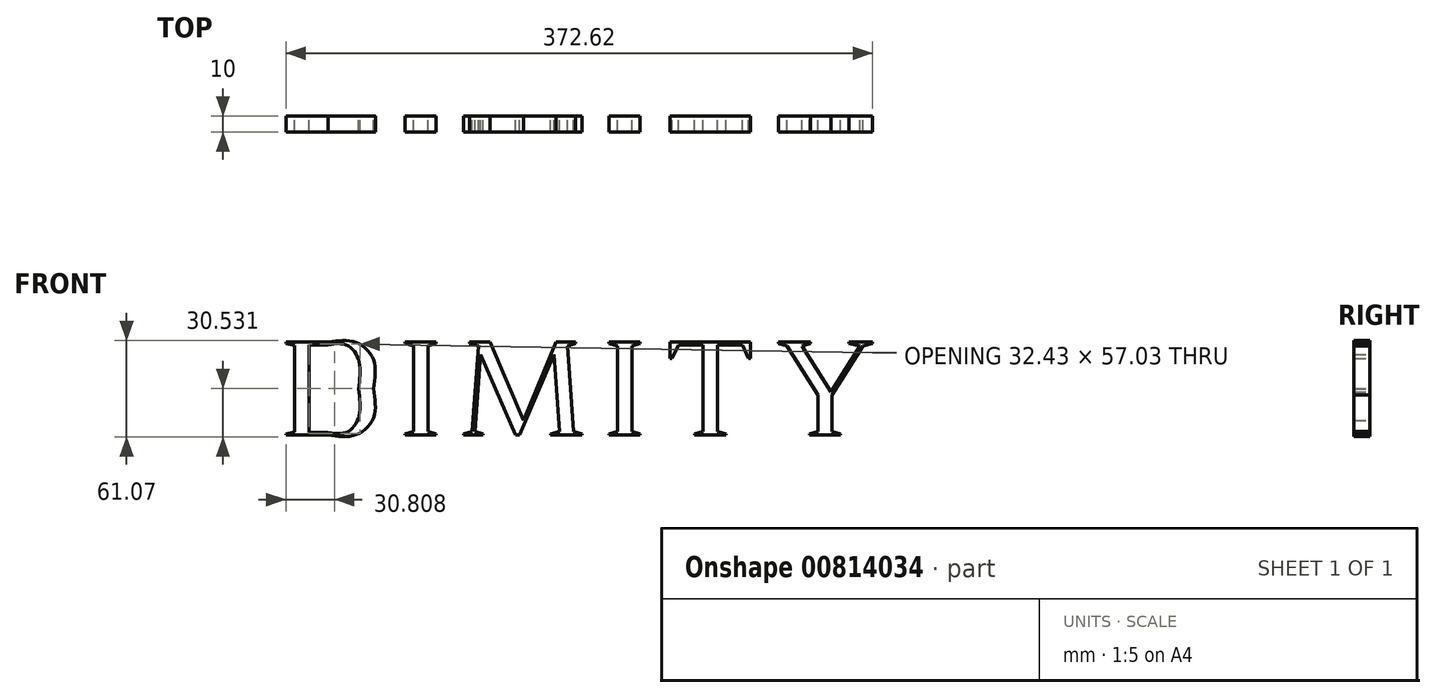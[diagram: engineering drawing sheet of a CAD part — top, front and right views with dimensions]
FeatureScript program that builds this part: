
annotation { "Feature Type Name" : "Feature", "Feature Type Description" : "" }
export const myFeature = defineFeature(function(context is Context, id is Id, definition is map)
    precondition{}
    {
        {
            var Q0;
            Q0=qCreatedBy(makeId("Front.planeOp"),FACE);
            var sketch = newSketch(context, id + "F0", { "sketchPlane" : qUnion([Q0])});
            skLineSegment(sketch, "E0", {"start": v(-186.3, 70.11) * mm, "end": v(-186.3, 69.35) * mm});
            skLineSegment(sketch, "E1", {"start": v(-186.3, 69.35) * mm, "end": v(-180.83, 68.09) * mm});
            skLineSegment(sketch, "E2", {"start": v(-180.83, 68.09) * mm, "end": v(-180.83, 13.09) * mm});
            skLineSegment(sketch, "E3", {"start": v(-180.83, 13.09) * mm, "end": v(-186.3, 11.74) * mm});
            skLineSegment(sketch, "E4", {"start": v(-186.3, 11.74) * mm, "end": v(-186.3, 11.06) * mm});
            skLineSegment(sketch, "E5", {"start": v(-186.3, 11.06) * mm, "end": v(-159.4, 11.06) * mm});
            skFitSpline(sketch, "E6", {"points": [v(-159.4, 11.06) * mm, v(-142.53, 11.06) * mm, v(-130.72, 22.03) * mm, v(-130.72, 40.59) * mm]});
            skFitSpline(sketch, "E7", {"points": [v(-130.72, 40.59) * mm, v(-130.72, 58.98) * mm, v(-142.53, 70.11) * mm, v(-159.4, 70.11) * mm]});
            skLineSegment(sketch, "E8", {"start": v(-159.4, 70.11) * mm, "end": v(-186.3, 70.11) * mm});
            skLineSegment(sketch, "E9", {"start": v(-171.72, 68.43) * mm, "end": v(-159.4, 68.43) * mm});
            skFitSpline(sketch, "E10", {"points": [v(-159.4, 68.43) * mm, v(-148.26, 68.43) * mm, v(-140.25, 59.15) * mm, v(-140.25, 40.5) * mm]});
            skFitSpline(sketch, "E11", {"points": [v(-140.25, 40.5) * mm, v(-140.25, 21.95) * mm, v(-148.26, 12.75) * mm, v(-159.4, 12.75) * mm]});
            skLineSegment(sketch, "E12", {"start": v(-159.4, 12.75) * mm, "end": v(-171.72, 12.75) * mm});
            skLineSegment(sketch, "E13", {"start": v(-171.72, 12.75) * mm, "end": v(-171.72, 68.43) * mm});
            skLineSegment(sketch, "E14", {"start": v(-110.64, 70.11) * mm, "end": v(-110.64, 69.27) * mm});
            skLineSegment(sketch, "E15", {"start": v(-110.64, 69.27) * mm, "end": v(-105.15, 67.67) * mm});
            skLineSegment(sketch, "E16", {"start": v(-105.15, 67.67) * mm, "end": v(-105.15, 13.5) * mm});
            skLineSegment(sketch, "E17", {"start": v(-105.15, 13.5) * mm, "end": v(-110.64, 11.9) * mm});
            skLineSegment(sketch, "E18", {"start": v(-110.64, 11.9) * mm, "end": v(-110.64, 11.06) * mm});
            skLineSegment(sketch, "E19", {"start": v(-110.64, 11.06) * mm, "end": v(-90.98, 11.06) * mm});
            skLineSegment(sketch, "E20", {"start": v(-90.98, 11.06) * mm, "end": v(-90.98, 11.9) * mm});
            skLineSegment(sketch, "E21", {"start": v(-90.98, 11.9) * mm, "end": v(-96.21, 13.5) * mm});
            skLineSegment(sketch, "E22", {"start": v(-96.21, 13.5) * mm, "end": v(-96.21, 67.67) * mm});
            skLineSegment(sketch, "E23", {"start": v(-96.21, 67.67) * mm, "end": v(-90.98, 69.27) * mm});
            skLineSegment(sketch, "E24", {"start": v(-90.98, 69.27) * mm, "end": v(-90.98, 70.11) * mm});
            skLineSegment(sketch, "E25", {"start": v(-90.98, 70.11) * mm, "end": v(-110.64, 70.11) * mm});
            skLineSegment(sketch, "E26", {"start": v(-69.55, 70.11) * mm, "end": v(-69.55, 69.27) * mm});
            skLineSegment(sketch, "E27", {"start": v(-69.55, 69.27) * mm, "end": v(-64.07, 67.67) * mm});
            skLineSegment(sketch, "E28", {"start": v(-64.07, 67.67) * mm, "end": v(-68.04, 13.34) * mm});
            skLineSegment(sketch, "E29", {"start": v(-68.04, 13.34) * mm, "end": v(-73.52, 11.74) * mm});
            skLineSegment(sketch, "E30", {"start": v(-73.52, 11.74) * mm, "end": v(-73.52, 11.06) * mm});
            skLineSegment(sketch, "E31", {"start": v(-73.52, 11.06) * mm, "end": v(-61.12, 11.06) * mm});
            skLineSegment(sketch, "E32", {"start": v(-61.12, 11.06) * mm, "end": v(-61.12, 11.74) * mm});
            skLineSegment(sketch, "E33", {"start": v(-61.12, 11.74) * mm, "end": v(-66.27, 13.34) * mm});
            skLineSegment(sketch, "E34", {"start": v(-66.27, 13.34) * mm, "end": v(-62.64, 62.44) * mm});
            skLineSegment(sketch, "E35", {"start": v(-62.64, 62.44) * mm, "end": v(-40.62, 11.06) * mm});
            skLineSegment(sketch, "E36", {"start": v(-40.62, 11.06) * mm, "end": v(-37.84, 11.06) * mm});
            skLineSegment(sketch, "E37", {"start": v(-37.84, 11.06) * mm, "end": v(-16.16, 62.35) * mm});
            skLineSegment(sketch, "E38", {"start": v(-16.16, 62.35) * mm, "end": v(-12.61, 13.5) * mm});
            skLineSegment(sketch, "E39", {"start": v(-12.61, 13.5) * mm, "end": v(-18.1, 11.9) * mm});
            skLineSegment(sketch, "E40", {"start": v(-18.1, 11.9) * mm, "end": v(-18.1, 11.06) * mm});
            skLineSegment(sketch, "E41", {"start": v(-18.1, 11.06) * mm, "end": v(1.64, 11.06) * mm});
            skLineSegment(sketch, "E42", {"start": v(1.64, 11.06) * mm, "end": v(1.64, 11.9) * mm});
            skLineSegment(sketch, "E43", {"start": v(1.64, 11.9) * mm, "end": v(-3.59, 13.5) * mm});
            skLineSegment(sketch, "E44", {"start": v(-3.59, 13.5) * mm, "end": v(-7.47, 67.67) * mm});
            skLineSegment(sketch, "E45", {"start": v(-7.47, 67.67) * mm, "end": v(-2.24, 69.27) * mm});
            skLineSegment(sketch, "E46", {"start": v(-2.24, 69.27) * mm, "end": v(-2.24, 70.11) * mm});
            skLineSegment(sketch, "E47", {"start": v(-2.24, 70.11) * mm, "end": v(-14.64, 70.11) * mm});
            skLineSegment(sketch, "E48", {"start": v(-14.64, 70.11) * mm, "end": v(-35.56, 20.34) * mm});
            skLineSegment(sketch, "E49", {"start": v(-35.56, 20.34) * mm, "end": v(-56.65, 70.11) * mm});
            skLineSegment(sketch, "E50", {"start": v(-56.65, 70.11) * mm, "end": v(-69.55, 70.11) * mm});
            skLineSegment(sketch, "E51", {"start": v(18.94, 70.11) * mm, "end": v(18.94, 69.27) * mm});
            skLineSegment(sketch, "E52", {"start": v(18.94, 69.27) * mm, "end": v(24.42, 67.67) * mm});
            skLineSegment(sketch, "E53", {"start": v(24.42, 67.67) * mm, "end": v(24.42, 13.5) * mm});
            skLineSegment(sketch, "E54", {"start": v(24.42, 13.5) * mm, "end": v(18.94, 11.9) * mm});
            skLineSegment(sketch, "E55", {"start": v(18.94, 11.9) * mm, "end": v(18.94, 11.06) * mm});
            skLineSegment(sketch, "E56", {"start": v(18.94, 11.06) * mm, "end": v(38.6, 11.06) * mm});
            skLineSegment(sketch, "E57", {"start": v(38.6, 11.06) * mm, "end": v(38.6, 11.9) * mm});
            skLineSegment(sketch, "E58", {"start": v(38.6, 11.9) * mm, "end": v(33.37, 13.5) * mm});
            skLineSegment(sketch, "E59", {"start": v(33.37, 13.5) * mm, "end": v(33.37, 67.67) * mm});
            skLineSegment(sketch, "E60", {"start": v(33.37, 67.67) * mm, "end": v(38.6, 69.27) * mm});
            skLineSegment(sketch, "E61", {"start": v(38.6, 69.27) * mm, "end": v(38.6, 70.11) * mm});
            skLineSegment(sketch, "E62", {"start": v(38.6, 70.11) * mm, "end": v(18.94, 70.11) * mm});
            skLineSegment(sketch, "E63", {"start": v(57.66, 70.11) * mm, "end": v(57.66, 59.74) * mm});
            skLineSegment(sketch, "E64", {"start": v(57.66, 59.74) * mm, "end": v(59.01, 59.74) * mm});
            skLineSegment(sketch, "E65", {"start": v(59.01, 59.74) * mm, "end": v(62.98, 68.43) * mm});
            skLineSegment(sketch, "E66", {"start": v(62.98, 68.43) * mm, "end": v(78.67, 68.43) * mm});
            skLineSegment(sketch, "E67", {"start": v(78.67, 68.43) * mm, "end": v(78.67, 13.5) * mm});
            skLineSegment(sketch, "E68", {"start": v(78.67, 13.5) * mm, "end": v(73.18, 11.9) * mm});
            skLineSegment(sketch, "E69", {"start": v(73.18, 11.9) * mm, "end": v(73.18, 11.06) * mm});
            skLineSegment(sketch, "E70", {"start": v(73.18, 11.06) * mm, "end": v(93.26, 11.06) * mm});
            skLineSegment(sketch, "E71", {"start": v(93.26, 11.06) * mm, "end": v(93.26, 11.9) * mm});
            skLineSegment(sketch, "E72", {"start": v(93.26, 11.9) * mm, "end": v(87.78, 13.5) * mm});
            skLineSegment(sketch, "E73", {"start": v(87.78, 13.5) * mm, "end": v(87.78, 68.43) * mm});
            skLineSegment(sketch, "E74", {"start": v(87.78, 68.43) * mm, "end": v(103.55, 68.43) * mm});
            skLineSegment(sketch, "E75", {"start": v(103.55, 68.43) * mm, "end": v(107.43, 59.74) * mm});
            skLineSegment(sketch, "E76", {"start": v(107.43, 59.74) * mm, "end": v(108.87, 59.74) * mm});
            skLineSegment(sketch, "E77", {"start": v(108.87, 59.74) * mm, "end": v(108.87, 70.11) * mm});
            skLineSegment(sketch, "E78", {"start": v(108.87, 70.11) * mm, "end": v(57.66, 70.11) * mm});
            skLineSegment(sketch, "E79", {"start": v(126.58, 70.11) * mm, "end": v(126.58, 69.27) * mm});
            skLineSegment(sketch, "E80", {"start": v(126.58, 69.27) * mm, "end": v(131.81, 67.67) * mm});
            skLineSegment(sketch, "E81", {"start": v(131.81, 67.67) * mm, "end": v(151.55, 36.7) * mm});
            skLineSegment(sketch, "E82", {"start": v(151.55, 36.7) * mm, "end": v(151.55, 13.5) * mm});
            skLineSegment(sketch, "E83", {"start": v(151.55, 13.5) * mm, "end": v(146.07, 11.9) * mm});
            skLineSegment(sketch, "E84", {"start": v(146.07, 11.9) * mm, "end": v(146.07, 11.06) * mm});
            skLineSegment(sketch, "E85", {"start": v(146.07, 11.06) * mm, "end": v(165.8, 11.06) * mm});
            skLineSegment(sketch, "E86", {"start": v(165.8, 11.06) * mm, "end": v(165.8, 11.9) * mm});
            skLineSegment(sketch, "E87", {"start": v(165.8, 11.9) * mm, "end": v(160.58, 13.5) * mm});
            skLineSegment(sketch, "E88", {"start": v(160.58, 13.5) * mm, "end": v(160.58, 36.7) * mm});
            skLineSegment(sketch, "E89", {"start": v(160.58, 36.7) * mm, "end": v(180.32, 67.67) * mm});
            skLineSegment(sketch, "E90", {"start": v(180.32, 67.67) * mm, "end": v(186.3, 69.27) * mm});
            skLineSegment(sketch, "E91", {"start": v(186.3, 69.27) * mm, "end": v(186.3, 70.11) * mm});
            skLineSegment(sketch, "E92", {"start": v(186.3, 70.11) * mm, "end": v(171.3, 70.11) * mm});
            skLineSegment(sketch, "E93", {"start": v(171.3, 70.11) * mm, "end": v(171.3, 69.27) * mm});
            skLineSegment(sketch, "E94", {"start": v(171.3, 69.27) * mm, "end": v(178.38, 67.67) * mm});
            skLineSegment(sketch, "E95", {"start": v(178.38, 67.67) * mm, "end": v(159.74, 38.56) * mm});
            skLineSegment(sketch, "E96", {"start": v(159.74, 38.56) * mm, "end": v(141.35, 67.67) * mm});
            skLineSegment(sketch, "E97", {"start": v(141.35, 67.67) * mm, "end": v(146.91, 69.27) * mm});
            skLineSegment(sketch, "E98", {"start": v(146.91, 69.27) * mm, "end": v(146.91, 70.11) * mm});
            skLineSegment(sketch, "E99", {"start": v(146.91, 70.11) * mm, "end": v(126.58, 70.11) * mm});
            skSolve(sketch);
        }
        {
            var Q0;
            Q0 = qSketchRegion(id + "F0", true);
            extrude(context, id + "F1", {"entities" : qUnion([Q0]), "depth" : 10 * mm, "offsetDistance" : 25 * mm});
        }
    });
